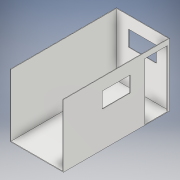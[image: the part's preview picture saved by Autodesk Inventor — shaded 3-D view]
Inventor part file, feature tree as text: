
AUTODESK INVENTOR PART (.ipt)
format: ipt  version: 2018 (Build 220112000, 112)  size: 188,416 bytes
history: native  units: mm
features: extrude x7, sketch x7, projected_geometry x1
ambient origin geometry x8: Origin, YZ Plane, XZ Plane, XY Plane, X Axis, Y Axis, Z Axis, Center Point
bodies: Volumenkörper1 (feature_tree)
feature tree (15):
  extrude  "Bodenplatte"  Depth=1.5mm
  extrude  "Wand_links"  Depth=150.0mm
  extrude  "Wand_rechts"  Depth=1.8mm TaperAngle=0.0deg
  extrude  "Wand_vorn"  Depth=180.0mm TaperAngle=0.0deg
  extrude  "Fenster_vorn"  Depth=180.0mm TaperAngle=0.0deg
  extrude  "Fenster_rechts"  Depth=180.0mm TaperAngle=0.0deg
  extrude  "Tuer_rechts"  Depth=45.4mm
  sketch  "Skizze1"  dims[d2=1.5mm d3=1.5mm]
  sketch  "Skizze3"  dims[d4=1.5mm d5=150.0mm]
  sketch  "Skizze4"  dims[d6=305.0mm d7=1.8mm d8=0.0mm]
  sketch  "Skizze5"  dims[d9=1.5mm d10=180.0mm d11=0.0mm]
  sketch  "Skizze6"  dims[d12=1.5mm d13=180.0mm d14=0.0mm]
  projected_geometry  "Projizierte Kontur1"
  sketch  "Skizze7"  dims[d15=1.5mm d16=180.0mm d17=0.0mm]
  sketch  "Skizze8"  dims[d18=80.4mm d19=45.4mm d21=10.0mm d22=0.0mm d25=100.0mm d26=45.4mm d27=80.4mm d28=1.2mm d29=1.2mm d30=1.2mm d31=1.2mm d32=10.0mm d33=0.0mm d34=100.0mm d35=1.2mm d36=65.0mm d37=165.0mm d38=5.0mm d40=10.0mm d41=0.0mm]
